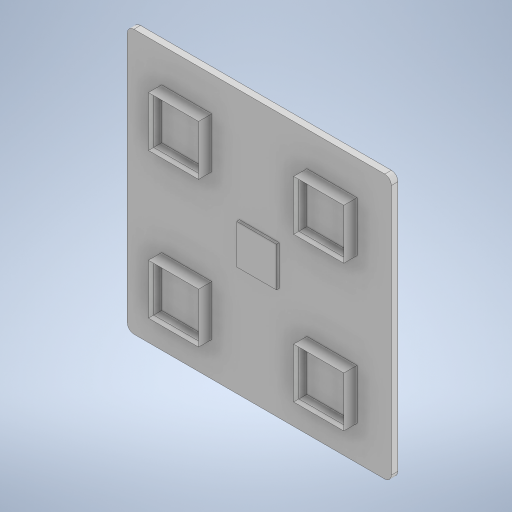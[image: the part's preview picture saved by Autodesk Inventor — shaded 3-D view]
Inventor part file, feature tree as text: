
AUTODESK INVENTOR PART (.ipt)
format: ipt  version: 2023 (Build 270158000, 158)  size: 350,720 bytes
history: native  units: mm
features: projected_geometry x7, extrude x3, sketch x3, other x1, fillet x1, chamfer x1
ambient origin geometry x8: Origin, YZ Plane, XZ Plane, XY Plane, X Axis, Y Axis, Z Axis, Center Point
bodies: Body1 (feature_tree)
feature tree (16):
  other  "Těleso1"
  extrude  "Vysunutí1"  Depth=200.0mm
  fillet  "Zaoblení1"  Radius=200.0mm
  extrude  "Vysunutí2"  Depth=5.0mm TaperAngle=0.0deg
  extrude  "Vysunutí3"  Depth=5.0mm
  chamfer  "Zkosení1"  Distance=30.0mm
  sketch  "Náčrt1"
  sketch  "Náčrt2"
  projected_geometry  "Promítnutá smyčka1"
  sketch  "Náčrt4"
  projected_geometry  "Promítnutá smyčka2"
  projected_geometry  "Promítnutá smyčka3"
  projected_geometry  "Promítnutá smyčka4"
  projected_geometry  "Promítnutá smyčka5"
  projected_geometry  "Promítnutá smyčka6"
  projected_geometry  "Promítnutá smyčka7"
